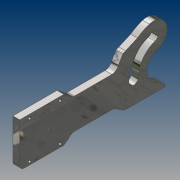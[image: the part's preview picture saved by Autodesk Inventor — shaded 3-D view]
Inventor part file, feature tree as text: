
AUTODESK INVENTOR PART (.ipt)
format: ipt  version: 2021 (Build 250183000, 183)  size: 240,640 bytes
history: native  units: mm
features: extrude x6, sketch x5, chamfer x3, fillet x3, hole x2, projected_geometry x2
ambient origin geometry x8: Origin, YZ Plane, XZ Plane, XY Plane, X Axis, Y Axis, Z Axis, Center Point
bodies: Solid1 (feature_tree)
feature tree (21):
  sketch  "Sketch1"  dims[d0=45.0mm d1=55.0mm]
  extrude  "Extrusion1"  Depth=55.0mm
  hole  "Hole1"  [1 undecoded]
  sketch  "Sketch3"  dims[d2=65.0mm d3=200.0mm]
  extrude  "Extrusion2"  Depth=10.0mm TaperAngle=0.0deg
  extrude  "Extrusion3"  Depth=2.0mm
  extrude  "Extrusion4"  Depth=10.0mm
  chamfer  "Chamfer1"  Distance=80.0mm
  fillet  "Fillet1"  Radius=7.2mm
  extrude  "Extrusion5"  Depth=10.0mm TaperAngle=0.0deg
  fillet  "Fillet2"  Radius=85.0mm
  hole  "Hole3"  [1 undecoded]
  extrude  "Extrusion6"  Depth=2.0mm TaperAngle=45.0deg
  chamfer  "Chamfer2"  Distance=119.0mm
  chamfer  "Chamfer3"  Distance=36.25mm
  fillet  "Fillet3"  Radius=2.0mm
  projected_geometry  "Projected Loop2"
  sketch  "Sketch4"  dims[d4=15.0mm d5=10.0mm d6=0.0mm]
  sketch  "Sketch5"  dims[d7=4.2mm d8=6.0mm d9=4.0mm d10=2.0mm d11=90.0deg d12=8.0mm d13=20.594885mm d27=42.0mm]
  sketch  "Sketch6"  dims[d28=20.0mm d29=10.0mm d30=80.0mm d32=7.2mm d33=10.0mm d34=0.0mm d35=85.0mm d36=0.0mm d37=85.0mm d38=0.0mm d39=24.0mm d40=2.0mm d41=45.0deg d42=119.0mm d43=36.25mm d44=0.0mm d45=2.0mm d46=10.0mm d47=1.8mm d48=6.0mm d49=4.0mm d50=2.0mm d51=90.0deg d52=8.0mm d53=20.594885mm d55=27.5mm d56=0.0mm d57=10.0mm d58=55.0mm d59=8.5mm d60=2.0mm d61=45.0deg d62=5.75mm d63=2.0mm d64=45.0deg d65=6.5mm]
  projected_geometry  "Projected Loop3"
note: 2 required parameter values undecoded (feature->parameter linkage not recoverable at this tier; creation-order binding heuristic only, values carry confidence <= 0.55)
